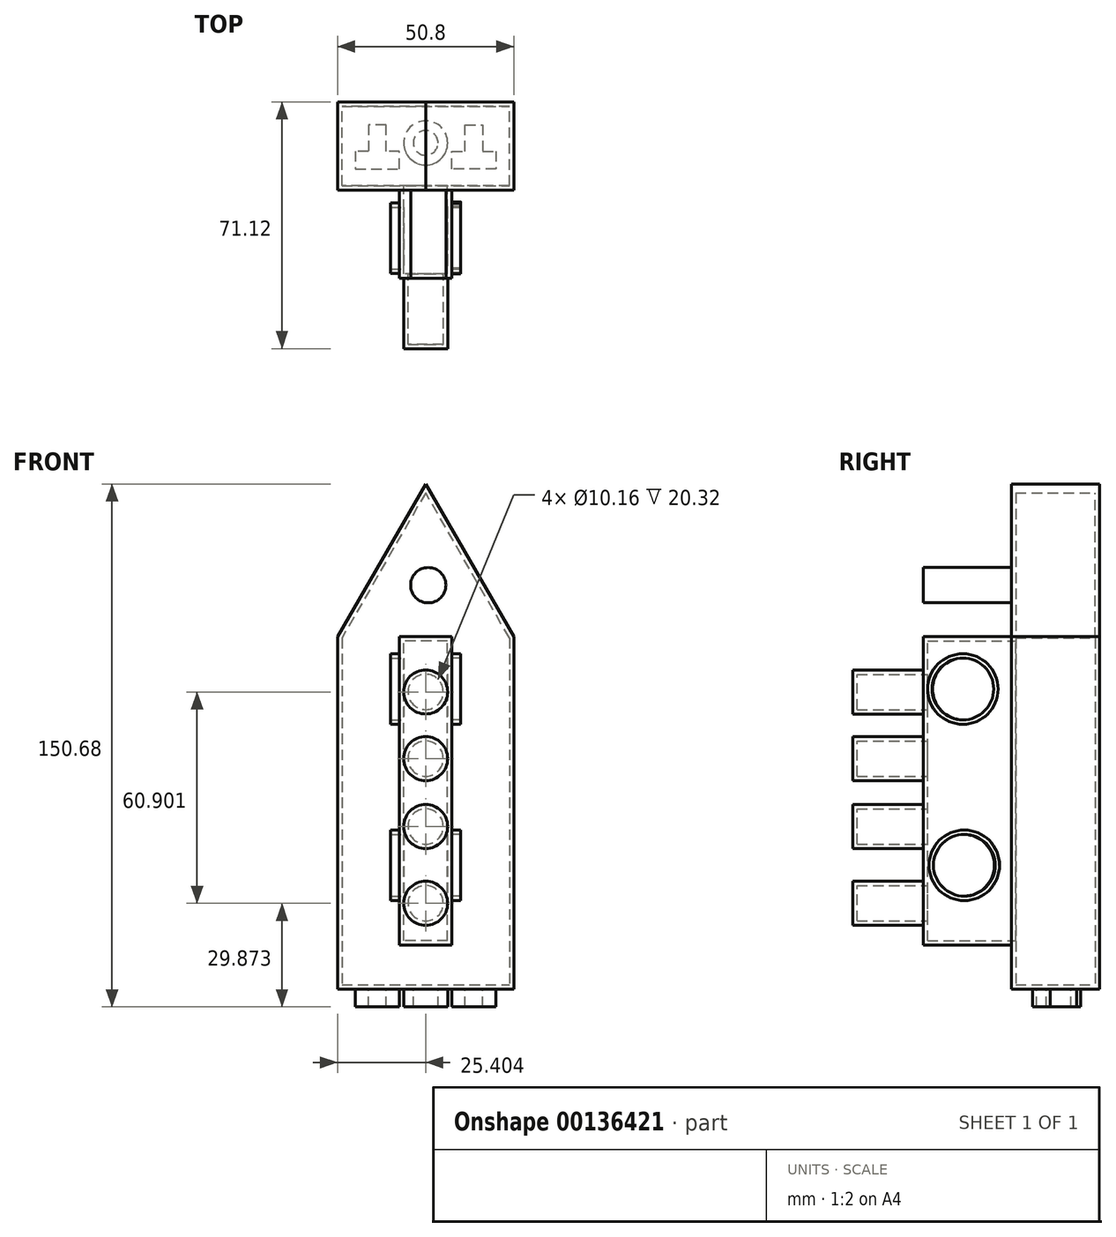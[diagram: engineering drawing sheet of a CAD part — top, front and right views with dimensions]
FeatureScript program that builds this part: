
annotation { "Feature Type Name" : "Feature", "Feature Type Description" : "" }
export const myFeature = defineFeature(function(context is Context, id is Id, definition is map)
    precondition{}
    {
        {
            var Q0;
            Q0=qCreatedBy(makeId("Front.planeOp"),FACE);
            var sketch = newSketch(context, id + "F0", { "sketchPlane" : qUnion([Q0])});
            skLineSegment(sketch, "E0.top", {"start": v(-17.84, -35.74) * mm, "end": v(32.96, -35.74) * mm});
            skLineSegment(sketch, "E0.left", {"start": v(-17.84, 65.86) * mm, "end": v(-17.84, -35.74) * mm});
            skLineSegment(sketch, "E0.right", {"start": v(32.96, 65.86) * mm, "end": v(32.96, -35.74) * mm});
            skLineSegment(sketch, "E1", {"start": v(32.96, 65.86) * mm, "end": v(7.56, 109.86) * mm});
            skLineSegment(sketch, "E2", {"start": v(7.56, 109.86) * mm, "end": v(-17.84, 65.86) * mm});
            skSolve(sketch);
        }
        {
            var Q0;
            Q0=makeQuery(id+"F0.imprint","IMPRINT",FACE,{"disambiguationData":[TD([[makeQuery(id+"F0.imprint","IMPRINT",EDGE,{"derivedFrom":sQuery(id+"F0.wireOp",EDGE,"E0.top")}),1.0]])]});
            extrude(context, id + "F1", {"entities" : qUnion([Q0]), "depth" : 25.4 * mm});
        }
        {
            var Q0;
            Q0=makeQuery(id+"F1.opExtrude","CAP_FACE",FACE,{"disambiguationData":[OSD([sQuery(id+"F0.wireOp",EDGE,"E0.top"),sQuery(id+"F0.wireOp",EDGE,"E0.left"),sQuery(id+"F0.wireOp",EDGE,"E0.right"),sQuery(id+"F0.wireOp",EDGE,"E1"),sQuery(id+"F0.wireOp",EDGE,"E2")])],"isStart":false});
            var sketch = newSketch(context, id + "F2", { "sketchPlane" : qUnion([Q0])});
            skLineSegment(sketch, "E3", {"start": v(15.13, -23.04) * mm, "end": v(0, -23.04) * mm});
            skLineSegment(sketch, "E4", {"start": v(15.13, -23.04) * mm, "end": v(15.13, 65.86) * mm});
            skLineSegment(sketch, "E5", {"start": v(0, -23.04) * mm, "end": v(0, 65.86) * mm});
            skLineSegment(sketch, "E6", {"start": v(15.13, 65.86) * mm, "end": v(0, 65.86) * mm});
            skSolve(sketch);
        }
        {
            var Q0;
            Q0=makeQuery(id+"F2.imprint","IMPRINT",FACE,{"disambiguationData":[TD([[makeQuery(id+"F2.imprint","IMPRINT",EDGE,{"derivedFrom":sQuery(id+"F2.wireOp",EDGE,"E3")}),-1.0]])]});
            extrude(context, id + "F3", {"entities" : qUnion([Q0]), "operationType" : NewBodyOperationType.ADD, "depth" : 25.4 * mm});
        }
        {
            var Q0;
            Q0=makeQuery(id+"F3.opExtrude","CAP_FACE",FACE,{"disambiguationData":[OSD([sQuery(id+"F2.wireOp",EDGE,"E3"),sQuery(id+"F2.wireOp",EDGE,"E4"),sQuery(id+"F2.wireOp",EDGE,"E5"),sQuery(id+"F2.wireOp",EDGE,"E6")])],"isStart":false});
            var sketch = newSketch(context, id + "F4", { "sketchPlane" : qUnion([Q0])});
            skCircle(sketch, "E7", {"center": v(7.56, -10.95) * mm, "radius": 6.35 * mm});
            skPoint(sketch, "E7.centerSnap0", {"position": v(7.56, 65.86) * mm});
            skCircle(sketch, "E8", {"center": v(7.56, 11.17) * mm, "radius": 6.35 * mm});
            skCircle(sketch, "E9", {"center": v(7.56, 30.74) * mm, "radius": 6.35 * mm});
            skCircle(sketch, "E10", {"center": v(7.56, 49.95) * mm, "radius": 6.35 * mm});
            skSolve(sketch);
        }
        {
            var Q0;
            Q0=makeQuery(id+"F4.imprint","IMPRINT",FACE,{"disambiguationData":[TD([[makeQuery(id+"F4.imprint","IMPRINT",EDGE,{"derivedFrom":sQuery(id+"F4.wireOp",EDGE,"E10")}),1.0]])]});
            var Q1;
            Q1=makeQuery(id+"F4.imprint","IMPRINT",FACE,{"disambiguationData":[TD([[makeQuery(id+"F4.imprint","IMPRINT",EDGE,{"derivedFrom":sQuery(id+"F4.wireOp",EDGE,"E9")}),1.0]])]});
            var Q2;
            Q2=makeQuery(id+"F4.imprint","IMPRINT",FACE,{"disambiguationData":[TD([[makeQuery(id+"F4.imprint","IMPRINT",EDGE,{"derivedFrom":sQuery(id+"F4.wireOp",EDGE,"E8")}),1.0]])]});
            var Q3;
            Q3=makeQuery(id+"F4.imprint","IMPRINT",FACE,{"disambiguationData":[TD([[makeQuery(id+"F4.imprint","IMPRINT",EDGE,{"derivedFrom":sQuery(id+"F4.wireOp",EDGE,"E7")}),1.0]])]});
            extrude(context, id + "F5", {"entities" : qUnion([Q0, Q1, Q2, Q3]), "operationType" : NewBodyOperationType.ADD, "depth" : 20.32 * mm});
        }
        {
            var Q0;
            Q0=makeQuery(id+"F3.opExtrude","SWEPT_FACE",FACE,{"disambiguationData":[OSD([sQuery(id+"F2.wireOp",EDGE,"E5")])]});
            var sketch = newSketch(context, id + "F6", { "sketchPlane" : qUnion([Q0])});
            skCircle(sketch, "E11", {"center": v(39.2, 0) * mm, "radius": 10.16 * mm});
            skCircle(sketch, "E12", {"center": v(39.2, 50.8) * mm, "radius": 10.16 * mm});
            skSolve(sketch);
        }
        {
            var Q0;
            Q0=makeQuery(id+"F3.opExtrude","SWEPT_FACE",FACE,{"disambiguationData":[OSD([sQuery(id+"F2.wireOp",EDGE,"E4")])]});
            var sketch = newSketch(context, id + "F7", { "sketchPlane" : qUnion([Q0])});
            skCircle(sketch, "E13", {"center": v(-39.38, 50.8) * mm, "radius": 10.16 * mm});
            skCircle(sketch, "E14", {"center": v(-38.95, 0) * mm, "radius": 10.16 * mm});
            skSolve(sketch);
        }
        {
            var Q0;
            Q0=makeQuery(id+"F7.imprint","IMPRINT",FACE,{"disambiguationData":[TD([[makeQuery(id+"F7.imprint","IMPRINT",EDGE,{"derivedFrom":sQuery(id+"F7.wireOp",EDGE,"E14")}),1.0]])]});
            var Q1;
            Q1=makeQuery(id+"F7.imprint","IMPRINT",FACE,{"disambiguationData":[TD([[makeQuery(id+"F7.imprint","IMPRINT",EDGE,{"derivedFrom":sQuery(id+"F7.wireOp",EDGE,"E13")}),1.0]])]});
            extrude(context, id + "F8", {"entities" : qUnion([Q0, Q1]), "operationType" : NewBodyOperationType.ADD, "depth" : 2.54 * mm});
        }
        {
            var Q0;
            Q0=makeQuery(id+"F6.imprint","IMPRINT",FACE,{"disambiguationData":[TD([[makeQuery(id+"F6.imprint","IMPRINT",EDGE,{"derivedFrom":sQuery(id+"F6.wireOp",EDGE,"E12")}),1.0]])]});
            var Q1;
            Q1=makeQuery(id+"F6.imprint","IMPRINT",FACE,{"disambiguationData":[TD([[makeQuery(id+"F6.imprint","IMPRINT",EDGE,{"derivedFrom":sQuery(id+"F6.wireOp",EDGE,"E11")}),1.0]])]});
            extrude(context, id + "F9", {"entities" : qUnion([Q0, Q1]), "operationType" : NewBodyOperationType.ADD, "depth" : 2.54 * mm});
        }
        {
            var Q0;
            Q0=makeQuery(id+"F8.opExtrude","CAP_FACE",FACE,{"disambiguationData":[OSD([sQuery(id+"F7.wireOp",EDGE,"E14")])],"isStart":false});
            var Q1;
            Q1=makeQuery(id+"F8.opExtrude","CAP_FACE",FACE,{"disambiguationData":[OSD([sQuery(id+"F7.wireOp",EDGE,"E13")])],"isStart":false});
            var Q2;
            Q2=makeQuery(id+"F9.opExtrude","CAP_FACE",FACE,{"disambiguationData":[OSD([sQuery(id+"F6.wireOp",EDGE,"E12")])],"isStart":false});
            var Q3;
            Q3=makeQuery(id+"F9.opExtrude","CAP_FACE",FACE,{"disambiguationData":[OSD([sQuery(id+"F6.wireOp",EDGE,"E11")])],"isStart":false});
            shell(context, id + "F10", {"entities" : qUnion([Q0, Q1, Q2, Q3]), "thickness" : 1.27 * mm});
        }
        {
            var Q0;
            Q0=makeQuery(id+"F1.opExtrude","SWEPT_FACE",FACE,{"disambiguationData":[OSD([sQuery(id+"F0.wireOp",EDGE,"E0.top")])]});
            var sketch = newSketch(context, id + "F11", { "sketchPlane" : qUnion([Q0])});
            skLineSegment(sketch, "E15", {"start": v(-12.7, 19.28) * mm, "end": v(0, 19.28) * mm});
            skLineSegment(sketch, "E16", {"start": v(0, 19.28) * mm, "end": v(0, 14.2) * mm});
            skLineSegment(sketch, "E17", {"start": v(0, 14.2) * mm, "end": v(-3.8, 14.2) * mm});
            skLineSegment(sketch, "E18", {"start": v(-3.8, 14.2) * mm, "end": v(-3.8, 6.58) * mm});
            skLineSegment(sketch, "E19", {"start": v(-3.8, 6.58) * mm, "end": v(-8.9, 6.58) * mm});
            skLineSegment(sketch, "E20", {"start": v(-8.9, 6.58) * mm, "end": v(-8.9, 14.2) * mm});
            skLineSegment(sketch, "E21", {"start": v(-8.9, 14.2) * mm, "end": v(-12.7, 14.2) * mm});
            skLineSegment(sketch, "E22", {"start": v(-12.7, 14.2) * mm, "end": v(-12.7, 19.28) * mm});
            skPoint(sketch, "E23.startSnap0", {"position": v(7.56, 25.4) * mm});
            skLineSegment(sketch, "E24", {"start": v(15.13, 19.28) * mm, "end": v(15.13, 14.2) * mm});
            skLineSegment(sketch, "E25", {"start": v(15.13, 14.2) * mm, "end": v(18.94, 14.2) * mm});
            skLineSegment(sketch, "E26", {"start": v(18.94, 14.2) * mm, "end": v(18.94, 6.58) * mm});
            skLineSegment(sketch, "E27", {"start": v(18.94, 6.58) * mm, "end": v(24.02, 6.58) * mm});
            skLineSegment(sketch, "E28", {"start": v(24.02, 6.58) * mm, "end": v(24.02, 14.2) * mm});
            skLineSegment(sketch, "E29", {"start": v(24.02, 14.2) * mm, "end": v(27.83, 14.2) * mm});
            skLineSegment(sketch, "E30", {"start": v(27.83, 14.2) * mm, "end": v(27.83, 19.28) * mm});
            skLineSegment(sketch, "E31", {"start": v(27.83, 19.28) * mm, "end": v(15.13, 19.28) * mm});
            skCircle(sketch, "E32", {"center": v(7.57, 11.81) * mm, "radius": 6.35 * mm});
            skCircle(sketch, "E33", {"center": v(7.57, 11.81) * mm, "radius": 3.56 * mm});
            skSolve(sketch);
        }
        {
            var Q0;
            Q0=makeQuery(id+"F11.imprint","IMPRINT",FACE,{"disambiguationData":[TD([[makeQuery(id+"F11.imprint","IMPRINT",EDGE,{"derivedFrom":sQuery(id+"F11.wireOp",EDGE,"E32")}),1.0]])]});
            var Q1;
            Q1=makeQuery(id+"F11.imprint","IMPRINT",FACE,{"disambiguationData":[TD([[makeQuery(id+"F11.imprint","IMPRINT",EDGE,{"derivedFrom":sQuery(id+"F11.wireOp",EDGE,"E15")}),-1.0]])]});
            var Q2;
            Q2=makeQuery(id+"F11.imprint","IMPRINT",FACE,{"disambiguationData":[TD([[makeQuery(id+"F11.imprint","IMPRINT",EDGE,{"derivedFrom":sQuery(id+"F11.wireOp",EDGE,"E24")}),1.0]])]});
            extrude(context, id + "F12", {"entities" : qUnion([Q0, Q1, Q2]), "operationType" : NewBodyOperationType.ADD, "depth" : 5.08 * mm});
        }
        {
            var Q0;
            Q0=makeQuery(id+"F2.imprint","IMPRINT",FACE,{"disambiguationData":[TD([[makeQuery(id+"F2.imprint","IMPRINT",EDGE,{"derivedFrom":sQuery(id+"F2.wireOp",EDGE,"E3")}),1.0]])]});
            var sketch = newSketch(context, id + "F13", { "sketchPlane" : qUnion([Q0])});
            skCircle(sketch, "E34", {"center": v(8.31, 80.72) * mm, "radius": 5.08 * mm});
            skSolve(sketch);
        }
        {
            var Q0;
            Q0=makeQuery(id+"F13.imprint","IMPRINT",FACE,{"disambiguationData":[TD([[makeQuery(id+"F13.imprint","IMPRINT",EDGE,{"derivedFrom":sQuery(id+"F13.wireOp",EDGE,"E34")}),1.0]])]});
            extrude(context, id + "F14", {"entities" : qUnion([Q0]), "operationType" : NewBodyOperationType.ADD, "depth" : 25.4 * mm});
        }
    });
